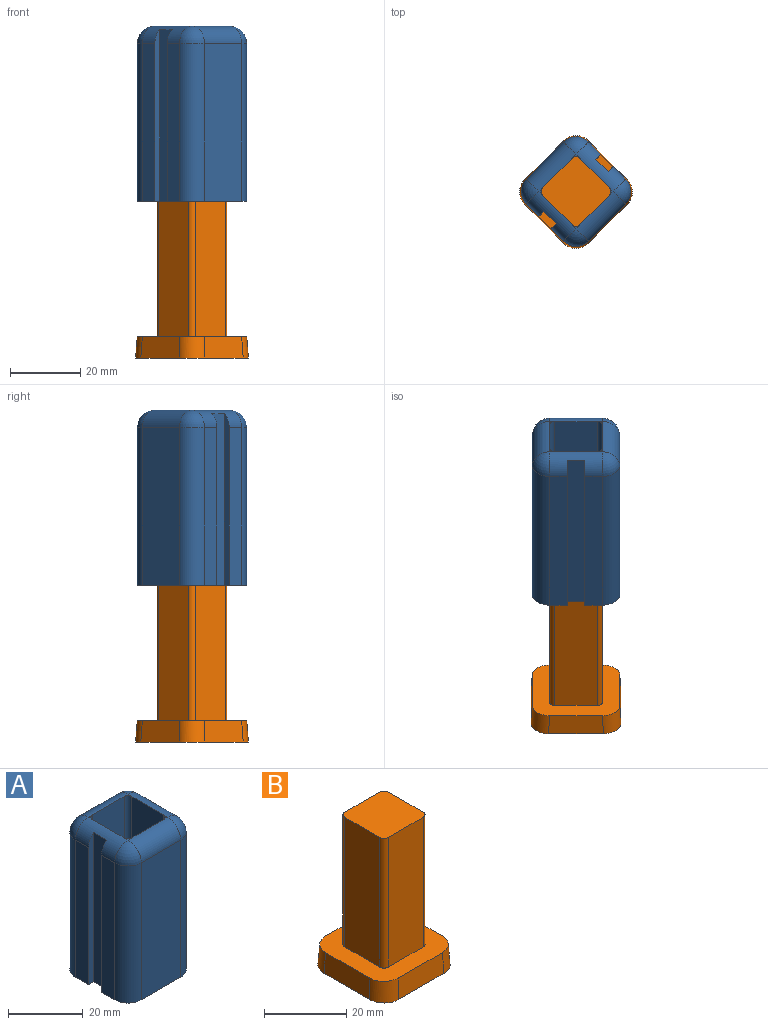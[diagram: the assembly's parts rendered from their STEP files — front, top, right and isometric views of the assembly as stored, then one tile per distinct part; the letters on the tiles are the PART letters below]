
ASSEMBLY  parts=2 mates=1
PART A: 37 faces, bbox 25x25x50 mm
  f0: plane 1.5x1.5mm, normal (0,0,1), area 0.5mm2, adj f13,f26,f27
  f1: plane 1.5x1.5mm, normal (0,0,1), area 0.5mm2, adj f11,f25,f26
  f2: plane 1.5x1.5mm, normal (0,0,1), area 0.5mm2, adj f7,f27,f28
  f3: plane 45x5mm, normal (-1,0,0), area 225mm2, adj f6,f19,f27,f35
  f4: plane 45x5mm, normal (-1,0,0), area 225mm2, adj f6,f20,f27,f33
  f5: plane 45x5mm, normal (1,0,0), area 225mm2, adj f6,f21,f25,f29
  f6: plane 25x25mm, normal (0,0,-1), area 360.5mm2, adj f3,f4,f5,f7,f8,f9,f10,f11
  f7: cylinder r=1.5mm len=50mm, axis (0,0,-1), area 117.8mm2, adj f2,f6,f8,f17
  f8: plane 50x12mm, normal (0,-1,0), area 600mm2, adj f6,f7,f9,f28
  f9: cylinder r=1.5mm len=50mm, axis (0,0,-1), area 117.8mm2, adj f6,f8,f10,f24
  f10: plane 50x12mm, normal (-1,0,0), area 600mm2, adj f6,f9,f11,f25
  f11: cylinder r=1.5mm len=50mm, axis (0,0,-1), area 117.8mm2, adj f1,f6,f10,f12
  f12: plane 50x12mm, normal (0,1,0), area 600mm2, adj f6,f11,f13,f26
  f13: cylinder r=1.5mm len=50mm, axis (0,0,-1), area 117.8mm2, adj f0,f6,f12,f17
  f14: plane 45x15mm, normal (0,-1,0), area 675mm2, adj f6,f26,f31,f33
  f15: plane 45x5mm, normal (1,0,0), area 225mm2, adj f6,f23,f25,f31
  f16: plane 45x15mm, normal (0,1,0), area 675mm2, adj f6,f28,f29,f35
  f17: plane 50x12mm, normal (1,0,0), area 600mm2, adj f6,f7,f13,f27
  f18: plane 49x5mm, normal (-1,0,0), area 245mm2, adj f6,f19,f20,f27
  f19: plane 49x2mm, normal (0,-1,0), area 95.6mm2, adj f3,f6,f18,f27
  f20: plane 49x2mm, normal (0,1,0), area 95.6mm2, adj f4,f6,f18,f27
  f21: plane 49x2mm, normal (0,-1,0), area 95.6mm2, adj f5,f6,f22,f25
  f22: plane 49x5mm, normal (1,0,0), area 245mm2, adj f6,f21,f23,f25
  f23: plane 49x2mm, normal (0,1,0), area 95.6mm2, adj f6,f15,f22,f25
  f24: plane 1.5x1.5mm, normal (0,0,1), area 0.5mm2, adj f9,f25,f28
  f25: cylinder r=5mm len=15mm, axis (0,-1,0), area 94.6mm2, adj f1,f5,f10,f15,f21,f22,f23,f24
  f26: cylinder r=5mm len=15mm, axis (-1,0,0), area 117.8mm2, adj f0,f1,f12,f14,f32,f34
  f27: cylinder r=5mm len=15mm, axis (0,1,0), area 94.6mm2, adj f0,f2,f3,f4,f17,f18,f19,f20
  f28: cylinder r=5mm len=15mm, axis (1,0,0), area 117.8mm2, adj f2,f8,f16,f24,f30,f36
  f29: cylinder r=5mm len=45mm, axis (0,0,-1), area 353.4mm2, adj f5,f6,f16,f30
  f30: sphere r=5mm, area 39.3mm2, adj f25,f28,f29
  f31: cylinder r=5mm len=45mm, axis (0,0,-1), area 353.4mm2, adj f6,f14,f15,f32
  f32: sphere r=5mm, area 39.3mm2, adj f25,f26,f31
  f33: cylinder r=5mm len=45mm, axis (0,0,-1), area 353.4mm2, adj f4,f6,f14,f34
  f34: sphere r=5mm, area 39.3mm2, adj f26,f27,f33
  f35: cylinder r=5mm len=45mm, axis (0,0,-1), area 353.4mm2, adj f3,f6,f16,f36
  f36: sphere r=5mm, area 39.3mm2, adj f27,f28,f35
PART B: 19 faces, bbox 25.7x25.7x44.8 mm
  f0: plane 25x25mm, normal (0,0,1), area 380.5mm2, adj f1,f2,f3,f4,f6,f7,f8,f9
  f1: plane 15.65x6.1mm, normal (-1,0,0.05), area 93.7mm2, adj f0,f5,f15,f18
  f2: plane 15.65x6.1mm, normal (0,-1,0.05), area 93.7mm2, adj f0,f5,f15,f16
  f3: plane 15.65x6.1mm, normal (1,0,0.05), area 93.7mm2, adj f0,f5,f16,f17
  f4: plane 15.65x6.1mm, normal (0,1,0.05), area 93.7mm2, adj f0,f5,f17,f18
  f5: plane 25.64x25.64mm, normal (0,0,-1), area 636mm2, adj f1,f2,f3,f4,f15,f16,f17,f18
  f6: plane 38.6x12mm, normal (0,1,0), area 463.2mm2, adj f0,f7,f13,f14
  f7: cylinder r=1.5mm len=38.6mm, axis (0,0,-1), area 90.9mm2, adj f0,f6,f8,f14
  f8: plane 38.6x12mm, normal (-1,0,0), area 463.2mm2, adj f0,f7,f9,f14
  f9: cylinder r=1.5mm len=38.6mm, axis (0,0,-1), area 90.9mm2, adj f0,f8,f10,f14
  f10: plane 38.6x12mm, normal (0,-1,0), area 463.2mm2, adj f0,f9,f11,f14
  f11: cylinder r=1.5mm len=38.6mm, axis (0,0,-1), area 90.9mm2, adj f0,f10,f12,f14
  f12: plane 38.6x12mm, normal (1,0,0), area 463.2mm2, adj f0,f11,f13,f14
  f13: cylinder r=1.5mm len=38.6mm, axis (0,0,-1), area 90.9mm2, adj f0,f6,f12,f14
  f14: plane 15x15mm, normal (0,0,1), area 223.1mm2, adj f6,f7,f8,f9,f10,f11,f12,f13
  f15: cylinder r=5mm len=6.32mm, axis (0.05,0.05,1), area 48mm2, adj f0,f1,f2,f5
  f16: cylinder r=5mm len=6.32mm, axis (-0.05,0.05,1), area 48mm2, adj f0,f2,f3,f5
  f17: cylinder r=5mm len=6.32mm, axis (-0.05,-0.05,1), area 48mm2, adj f0,f3,f4,f5
  f18: cylinder r=5mm len=6.32mm, axis (0.05,-0.05,1), area 48mm2, adj f0,f1,f4,f5
PLACE A rot(axis=(0,0,1),45deg) t=(12.5,-5.18,0)mm
PLACE B rot(axis=(0,0,1),45deg) t=(12.5,-5.18,-38.6)mm
MATE slider B.f14 <-> A.f6  axis (0,0,1) through (12.5,12.5,0)mm
